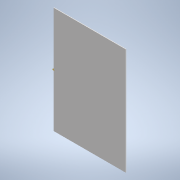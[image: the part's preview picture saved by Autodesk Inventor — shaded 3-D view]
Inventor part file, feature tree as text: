
AUTODESK INVENTOR PART (.ipt)
format: ipt  version: 2022 (Build 260153000, 153)  size: 90,112 bytes
history: native  units: in
note: dims shown in document units (in); Inventor stores cm internally (conversion verified against a paired STEP export)
features: extrude x1, other x1, sketch x1
ambient origin geometry x8: Origin, YZ Plane, XZ Plane, XY Plane, X Axis, Y Axis, Z Axis, Center Point
bodies: Solid1 (feature_tree)
feature tree (3):
  extrude  "Extrusion1"  [1 undecoded]
  other  "Work Point1"
  sketch  "Sketch1"  dims[d0=0.2362in d1=0.0in]
note: 1 required parameter value undecoded (feature->parameter linkage not recoverable at this tier; creation-order binding heuristic only, values carry confidence <= 0.55)
